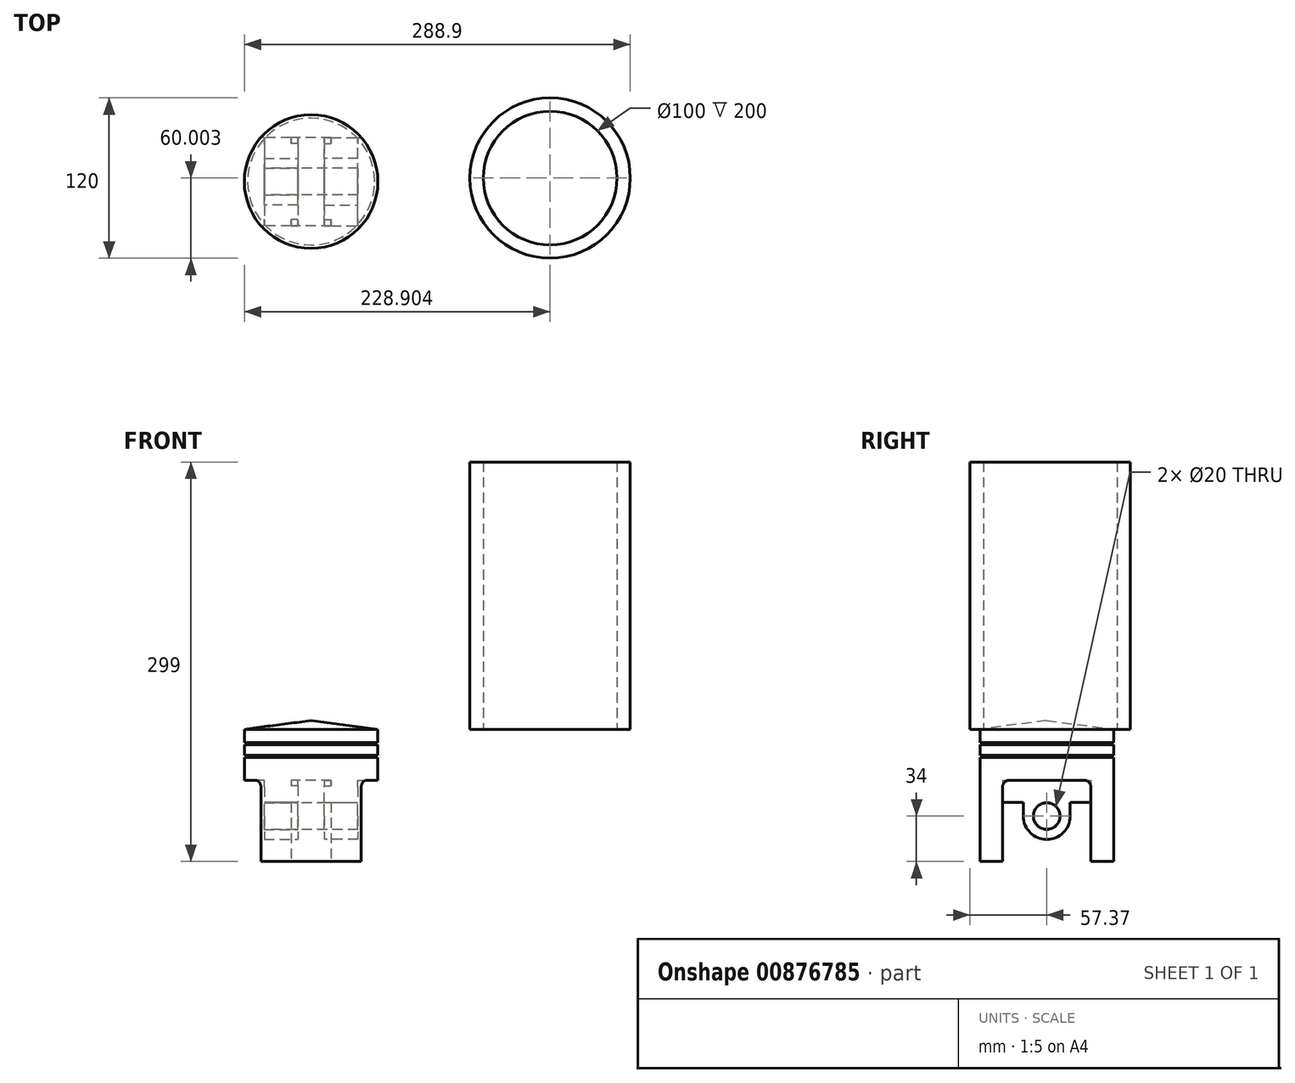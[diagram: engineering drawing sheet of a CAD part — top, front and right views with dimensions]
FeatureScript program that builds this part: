
annotation { "Feature Type Name" : "Feature", "Feature Type Description" : "" }
export const myFeature = defineFeature(function(context is Context, id is Id, definition is map)
    precondition{}
    {
        {
            var Q0;
            Q0=qCreatedBy(makeId("Top.planeOp"),FACE);
            var sketch = newSketch(context, id + "F0", { "sketchPlane" : qUnion([Q0])});
            skCircle(sketch, "E0", {"center": v(0, 0) * mm, "radius": 50 * mm});
            skSolve(sketch);
        }
        {
            var Q0;
            Q0=qCreatedBy(makeId("Right.planeOp"),FACE);
            var sketch = newSketch(context, id + "F1", { "sketchPlane" : qUnion([Q0])});
            skLineSegment(sketch, "E1", {"start": v(0, 0) * mm, "end": v(0, 6.5) * mm});
            skLineSegment(sketch, "E2", {"start": v(0, 6.5) * mm, "end": v(-50, 0) * mm});
            skLineSegment(sketch, "E3", {"start": v(-50, 0) * mm, "end": v(0, 0) * mm});
            skSolve(sketch);
        }
        {
            var Q0;
            Q0=makeQuery(id+"F1.imprint","IMPRINT",FACE,{"disambiguationData":[TD([[makeQuery(id+"F1.imprint","IMPRINT",EDGE,{"derivedFrom":sQuery(id+"F1.wireOp",EDGE,"E1")}),1.0]])]});
            var Q1;
            Q1=sQuery(id+"F1.wireOp",EDGE,"E1");
            revolve(context, id + "F2", {"surfaceOperationType" : NewSurfaceOperationType.NEW, "entities" : qUnion([Q0]), "axis" : qUnion([Q1]), "revolveType" : RevolveType.FULL});
        }
        {
            var Q0;
            Q0 = qSketchRegion(id + "F0", true);
            var Q1;
            Q1=sQuery(id+"F0.wireOp",EDGE,"E0");
            extrude(context, id + "F3", {"entities" : qUnion([Q0]), "surfaceEntities" : qUnion([Q1]), "oppositeDirection" : true, "depth" : 99 * mm, "offsetDistance" : 25 * mm});
        }
        {
            var Q0;
            Q0=qCreatedBy(makeId("Right.planeOp"),FACE);
            var sketch = newSketch(context, id + "F4", { "sketchPlane" : qUnion([Q0])});
            skLineSegment(sketch, "E4.bottom", {"start": v(-50, -10) * mm, "end": v(-47.5, -10) * mm});
            skLineSegment(sketch, "E4.top", {"start": v(-50, -11.5) * mm, "end": v(-47.5, -11.5) * mm});
            skLineSegment(sketch, "E4.left", {"start": v(-50, -10) * mm, "end": v(-50, -11.5) * mm});
            skLineSegment(sketch, "E4.right", {"start": v(-47.5, -10) * mm, "end": v(-47.5, -11.5) * mm});
            skLineSegment(sketch, "E5.bottom", {"start": v(-50, -19.5) * mm, "end": v(-47.5, -19.5) * mm});
            skLineSegment(sketch, "E5.top", {"start": v(-50, -21) * mm, "end": v(-47.5, -21) * mm});
            skLineSegment(sketch, "E5.left", {"start": v(-50, -19.5) * mm, "end": v(-50, -21) * mm});
            skLineSegment(sketch, "E5.right", {"start": v(-47.5, -19.5) * mm, "end": v(-47.5, -21) * mm});
            skSolve(sketch);
        }
        {
            var Q0;
            Q0=qCreatedBy(makeId("Right.planeOp"),FACE);
            var sketch = newSketch(context, id + "F5", { "sketchPlane" : qUnion([Q0])});
            skCircle(sketch, "E6", {"center": v(0, -57.38) * mm, "radius": 10 * mm});
            skSolve(sketch);
        }
        {
            var Q0;
            Q0 = qSketchRegion(id + "F4", true);
            var Q1;
            Q1=makeQuery(id+"F3.opExtrude","SWEPT_FACE",FACE,{"disambiguationData":[OSD([sQuery(id+"F0.wireOp",EDGE,"E0")])]});
            revolve(context, id + "F6", {"operationType" : NewBodyOperationType.REMOVE, "surfaceOperationType" : NewSurfaceOperationType.NEW, "entities" : qUnion([Q0]), "axis" : qUnion([Q1]), "revolveType" : RevolveType.FULL, "oppositeDirection" : true});
        }
        {
            var Q0;
            Q0=qCreatedBy(makeId("Right.planeOp"),FACE);
            cPlane(context, id + "F7", {"entities" : qUnion([Q0]), "cplaneType" : CPlaneType.OFFSET, "offset" : 50 * mm, "width" : 150 * mm, "height" : 150 * mm});
        }
        {
            var Q0;
            Q0=qCreatedBy(makeId("Right.planeOp"),FACE);
            cPlane(context, id + "F8", {"entities" : qUnion([Q0]), "cplaneType" : CPlaneType.OFFSET, "offset" : 50 * mm, "oppositeDirection" : true, "width" : 150 * mm, "height" : 150 * mm});
        }
        {
            var Q0;
            Q0=qCreatedBy(id+"F7.planeOp",FACE);
            var sketch = newSketch(context, id + "F9", { "sketchPlane" : qUnion([Q0])});
            skLineSegment(sketch, "E7.bottom", {"start": v(-33.06, -99) * mm, "end": v(33.06, -99) * mm});
            skLineSegment(sketch, "E7.top", {"start": v(-28.06, -38.19) * mm, "end": v(28.06, -38.19) * mm});
            skLineSegment(sketch, "E7.left", {"start": v(-33.06, -99) * mm, "end": v(-33.06, -43.19) * mm});
            skLineSegment(sketch, "E7.right", {"start": v(33.06, -99) * mm, "end": v(33.06, -43.19) * mm});
            skPoint(sketch, "E8.visualSharp", {"position": v(-33.06, -38.19) * mm});
            skArc(sketch, "E8.filletArc", {"start": v(-28.06, -38.19) * mm, "mid": v(-31.6, -39.65) * mm, "end": v(-33.06, -43.19) * mm});
            skPoint(sketch, "E9.visualSharp", {"position": v(33.06, -38.19) * mm});
            skArc(sketch, "E9.filletArc", {"start": v(33.06, -43.19) * mm, "mid": v(31.6, -39.65) * mm, "end": v(28.06, -38.19) * mm});
            skSolve(sketch);
        }
        {
            var Q0;
            Q0=makeQuery(id+"F9.imprint","IMPRINT",FACE,{"disambiguationData":[TD([[makeQuery(id+"F9.imprint","IMPRINT",EDGE,{"derivedFrom":sQuery(id+"F9.wireOp",EDGE,"E7.bottom")}),1.0]])]});
            extrude(context, id + "F10", {"entities" : qUnion([Q0]), "operationType" : NewBodyOperationType.REMOVE, "oppositeDirection" : true, "depth" : 35 * mm, "offsetDistance" : 25 * mm});
        }
        {
            var Q0;
            Q0=qCreatedBy(id+"F8.planeOp",FACE);
            var sketch = newSketch(context, id + "F11", { "sketchPlane" : qUnion([Q0])});
            skLineSegment(sketch, "E10.bottom", {"start": v(-28.06, -38.19) * mm, "end": v(28.06, -38.19) * mm});
            skLineSegment(sketch, "E10.top", {"start": v(-33.06, -99) * mm, "end": v(33.06, -99) * mm});
            skLineSegment(sketch, "E10.left", {"start": v(-33.06, -43.19) * mm, "end": v(-33.06, -99) * mm});
            skLineSegment(sketch, "E10.right", {"start": v(33.06, -43.19) * mm, "end": v(33.06, -99) * mm});
            skPoint(sketch, "E11.visualSharp", {"position": v(-33.06, -38.19) * mm});
            skArc(sketch, "E11.filletArc", {"start": v(-28.06, -38.19) * mm, "mid": v(-31.6, -39.65) * mm, "end": v(-33.06, -43.19) * mm});
            skPoint(sketch, "E12.visualSharp", {"position": v(33.06, -38.19) * mm});
            skArc(sketch, "E12.filletArc", {"start": v(33.06, -43.19) * mm, "mid": v(31.6, -39.65) * mm, "end": v(28.06, -38.19) * mm});
            skSolve(sketch);
        }
        {
            var Q0;
            Q0=makeQuery(id+"F11.imprint","IMPRINT",FACE,{"disambiguationData":[TD([[makeQuery(id+"F11.imprint","IMPRINT",EDGE,{"derivedFrom":sQuery(id+"F11.wireOp",EDGE,"E10.bottom")}),-1.0]])]});
            extrude(context, id + "F12", {"entities" : qUnion([Q0]), "operationType" : NewBodyOperationType.REMOVE, "depth" : 35 * mm, "offsetDistance" : 25 * mm});
        }
        {
            var Q0;
            Q0=makeQuery(id+"F5.imprint","IMPRINT",FACE,{"disambiguationData":[TD([[makeQuery(id+"F5.imprint","IMPRINT",EDGE,{"derivedFrom":sQuery(id+"F5.wireOp",EDGE,"E6")}),1.0]])]});
            var Q1;
            Q1=sQuery(id+"F5.wireOp",EDGE,"E6");
            extrude(context, id + "F13", {"entities" : qUnion([Q0]), "surfaceEntities" : qUnion([Q1]), "endBound" : BoundingType.SYMMETRIC, "depth" : 39.6 * mm, "offsetDistance" : 25 * mm});
        }
        {
            var Q0;
            Q0=makeQuery(id+"F13.opExtrude","SWEPT_BODY",BODY,{"disambiguationData":[OSD([sQuery(id+"F5.wireOp",EDGE,"E6")])]});
            var Q1;
            Q1=makeQuery(id+"F3.opExtrude","SWEPT_BODY",BODY,{"disambiguationData":[OSD([sQuery(id+"F0.wireOp",EDGE,"E0")])]});
            booleanBodies(context, id + "F14", {"operationType" : BooleanOperationType.SUBTRACTION, "tools" : qUnion([Q0]), "targets" : qUnion([Q1])});
        }
        {
            var Q0;
            Q0=makeQuery(id+"F3.opExtrude","CAP_FACE",FACE,{"disambiguationData":[OSD([sQuery(id+"F0.wireOp",EDGE,"E0")])],"isStart":false});
            var sketch = newSketch(context, id + "F15", { "sketchPlane" : qUnion([Q0])});
            skLineSegment(sketch, "E13.bottom", {"start": v(15, -33) * mm, "end": v(-15, -33) * mm});
            skLineSegment(sketch, "E13.top", {"start": v(15, 33) * mm, "end": v(-15, 33) * mm});
            skLineSegment(sketch, "E13.left", {"start": v(15, -33) * mm, "end": v(15, 33) * mm});
            skLineSegment(sketch, "E13.right", {"start": v(-15, -33) * mm, "end": v(-15, 33) * mm});
            skSolve(sketch);
        }
        {
            var Q0;
            Q0 = qSketchRegion(id + "F15", true);
            extrude(context, id + "F16", {"entities" : qUnion([Q0]), "operationType" : NewBodyOperationType.REMOVE, "oppositeDirection" : true, "depth" : 60.8 * mm, "offsetDistance" : 25 * mm});
        }
        {
            var Q0;
            Q0 = qSketchRegion(id + "F15", true);
            extrude(context, id + "F17", {"entities" : qUnion([Q0]), "operationType" : NewBodyOperationType.REMOVE, "oppositeDirection" : true, "depth" : 60 * mm, "offsetDistance" : 25 * mm});
        }
        {
            var Q0;
            Q0=qCreatedBy(makeId("Right.planeOp"),FACE);
            cPlane(context, id + "F18", {"entities" : qUnion([Q0]), "cplaneType" : CPlaneType.OFFSET, "offset" : 10 * mm, "width" : 150 * mm, "height" : 150 * mm});
        }
        {
            var Q0;
            Q0=qCreatedBy(makeId("Right.planeOp"),FACE);
            cPlane(context, id + "F19", {"entities" : qUnion([Q0]), "cplaneType" : CPlaneType.OFFSET, "offset" : 10 * mm, "oppositeDirection" : true, "width" : 150 * mm, "height" : 150 * mm});
        }
        {
            var Q0;
            Q0=qCreatedBy(id+"F18.planeOp",FACE);
            var sketch = newSketch(context, id + "F20", { "sketchPlane" : qUnion([Q0])});
            skCircle(sketch, "E14", {"center": v(0, -65) * mm, "radius": 10 * mm});
            skArc(sketch, "E15", {"start": v(-17.5, -65) * mm, "mid": v(0, -82.5) * mm, "end": v(17.5, -65) * mm});
            skLineSegment(sketch, "E16", {"start": v(-17.5, -65) * mm, "end": v(-17.5, -38.2) * mm});
            skLineSegment(sketch, "E17", {"start": v(17.5, -65) * mm, "end": v(17.5, -38.2) * mm});
            skLineSegment(sketch, "E18", {"start": v(17.5, -38.2) * mm, "end": v(-17.5, -38.2) * mm});
            skSolve(sketch);
        }
        {
            var Q0;
            Q0=qCreatedBy(id+"F19.planeOp",FACE);
            var sketch = newSketch(context, id + "F21", { "sketchPlane" : qUnion([Q0])});
            skCircle(sketch, "E19", {"center": v(0, -65) * mm, "radius": 10 * mm});
            skArc(sketch, "E20", {"start": v(-17.5, -65) * mm, "mid": v(0, -82.5) * mm, "end": v(17.5, -65) * mm});
            skLineSegment(sketch, "E21", {"start": v(-17.5, -65) * mm, "end": v(-17.5, -38.2) * mm});
            skLineSegment(sketch, "E22", {"start": v(17.5, -65) * mm, "end": v(17.5, -38.2) * mm});
            skLineSegment(sketch, "E23", {"start": v(17.5, -38.2) * mm, "end": v(-17.5, -38.2) * mm});
            skSolve(sketch);
        }
        {
            var Q0;
            Q0 = qSketchRegion(id + "F20", true);
            extrude(context, id + "F22", {"entities" : qUnion([Q0]), "operationType" : NewBodyOperationType.ADD, "depth" : 25 * mm, "offsetDistance" : 25 * mm});
        }
        {
            var Q0;
            Q0 = qSketchRegion(id + "F21", true);
            extrude(context, id + "F23", {"entities" : qUnion([Q0]), "operationType" : NewBodyOperationType.ADD, "oppositeDirection" : true, "depth" : 25 * mm, "offsetDistance" : 25 * mm});
        }
        {
            var Q0;
            Q0=makeQuery(id+"F23.opExtrude","CAP_FACE",FACE,{"disambiguationData":[OSD([sQuery(id+"F21.wireOp",EDGE,"E19"),sQuery(id+"F21.wireOp",EDGE,"E20"),sQuery(id+"F21.wireOp",EDGE,"E21"),sQuery(id+"F21.wireOp",EDGE,"E22"),sQuery(id+"F21.wireOp",EDGE,"E23")])],"isStart":false});
            var sketch = newSketch(context, id + "F24", { "sketchPlane" : qUnion([Q0])});
            skLineSegment(sketch, "E24.bottom", {"start": v(-28.06, -38.19) * mm, "end": v(28.06, -38.19) * mm});
            skLineSegment(sketch, "E24.top", {"start": v(-33.06, -54.79) * mm, "end": v(33.06, -54.79) * mm});
            skLineSegment(sketch, "E24.left", {"start": v(-33.06, -43.19) * mm, "end": v(-33.06, -54.79) * mm});
            skLineSegment(sketch, "E24.right", {"start": v(33.06, -43.19) * mm, "end": v(33.06, -54.79) * mm});
            skPoint(sketch, "E25.visualSharp", {"position": v(-33.06, -38.19) * mm});
            skArc(sketch, "E25.filletArc", {"start": v(-28.06, -38.19) * mm, "mid": v(-31.6, -39.65) * mm, "end": v(-33.06, -43.19) * mm});
            skPoint(sketch, "E26.visualSharp", {"position": v(33.06, -38.19) * mm});
            skArc(sketch, "E26.filletArc", {"start": v(33.06, -43.19) * mm, "mid": v(31.6, -39.65) * mm, "end": v(28.06, -38.19) * mm});
            skSolve(sketch);
        }
        {
            var Q0;
            Q0=qCreatedBy(makeId("Right.planeOp"),FACE);
            cPlane(context, id + "F25", {"entities" : qUnion([Q0]), "cplaneType" : CPlaneType.OFFSET, "offset" : 35 * mm, "width" : 150 * mm, "height" : 150 * mm});
        }
        {
            var Q0;
            Q0=qCreatedBy(id+"F25.planeOp",FACE);
            var sketch = newSketch(context, id + "F26", { "sketchPlane" : qUnion([Q0])});
            skLineSegment(sketch, "E27.bottom", {"start": v(-28.06, -38.19) * mm, "end": v(28.06, -38.19) * mm});
            skLineSegment(sketch, "E27.top", {"start": v(-33.06, -54.79) * mm, "end": v(33.06, -54.79) * mm});
            skLineSegment(sketch, "E27.left", {"start": v(-33.06, -43.19) * mm, "end": v(-33.06, -54.79) * mm});
            skLineSegment(sketch, "E27.right", {"start": v(33.06, -43.19) * mm, "end": v(33.06, -54.79) * mm});
            skPoint(sketch, "E28.visualSharp", {"position": v(-33.06, -38.19) * mm});
            skArc(sketch, "E28.filletArc", {"start": v(-28.06, -38.19) * mm, "mid": v(-31.6, -39.65) * mm, "end": v(-33.06, -43.19) * mm});
            skPoint(sketch, "E29.visualSharp", {"position": v(33.06, -38.19) * mm});
            skArc(sketch, "E29.filletArc", {"start": v(33.06, -43.19) * mm, "mid": v(31.6, -39.65) * mm, "end": v(28.06, -38.19) * mm});
            skSolve(sketch);
        }
        {
            var Q0;
            Q0 = qSketchRegion(id + "F24", true);
            extrude(context, id + "F27", {"entities" : qUnion([Q0]), "operationType" : NewBodyOperationType.ADD, "oppositeDirection" : true, "depth" : 25 * mm, "offsetDistance" : 25 * mm});
        }
        {
            var Q0;
            Q0 = qSketchRegion(id + "F26", true);
            extrude(context, id + "F28", {"entities" : qUnion([Q0]), "operationType" : NewBodyOperationType.ADD, "oppositeDirection" : true, "depth" : 25 * mm, "offsetDistance" : 25 * mm});
        }
        {
            var Q0;
            Q0=qCreatedBy(makeId("Right.planeOp"),FACE);
            var sketch = newSketch(context, id + "F29", { "sketchPlane" : qUnion([Q0])});
            skCircle(sketch, "E30", {"center": v(0, -65) * mm, "radius": 9.95 * mm});
            skSolve(sketch);
        }
        {
            var Q0;
            Q0 = qSketchRegion(id + "F29", true);
            extrude(context, id + "F30", {"entities" : qUnion([Q0]), "endBound" : BoundingType.SYMMETRIC, "depth" : 70 * mm, "offsetDistance" : 25 * mm});
        }
        {
            var Q0;
            Q0=qCreatedBy(makeId("Top.planeOp"),FACE);
            var sketch = newSketch(context, id + "F31", { "sketchPlane" : qUnion([Q0])});
            skCircle(sketch, "E31", {"center": v(170.9, -5.84) * mm, "radius": 60 * mm});
            skSolve(sketch);
        }
        {
            var Q0;
            Q0=makeQuery(id+"F31.imprint","IMPRINT",FACE,{"disambiguationData":[TD([[makeQuery(id+"F31.imprint","IMPRINT",EDGE,{"derivedFrom":sQuery(id+"F31.wireOp",EDGE,"E31")}),1.0]])]});
            extrude(context, id + "F32", {"entities" : qUnion([Q0]), "depth" : 250 * mm, "offsetDistance" : 25 * mm});
        }
        {
            var Q0;
            Q0=makeQuery(id+"F32.opExtrude","CAP_FACE",FACE,{"disambiguationData":[OSD([sQuery(id+"F31.wireOp",EDGE,"E31")])],"isStart":false});
            var sketch = newSketch(context, id + "F33", { "sketchPlane" : qUnion([Q0])});
            skCircle(sketch, "E32", {"center": v(170.9, -5.84) * mm, "radius": 50 * mm});
            skSolve(sketch);
        }
        {
            var Q0;
            Q0=makeQuery(id+"F33.imprint","IMPRINT",FACE,{"disambiguationData":[TD([[makeQuery(id+"F33.imprint","IMPRINT",EDGE,{"derivedFrom":sQuery(id+"F33.wireOp",EDGE,"E32")}),1.0]])]});
            extrude(context, id + "F34", {"entities" : qUnion([Q0]), "operationType" : NewBodyOperationType.REMOVE, "oppositeDirection" : true, "depth" : 250 * mm, "offsetDistance" : 25 * mm});
        }
        {
            var Q0;
            Q0=makeQuery(id+"F32.opExtrude","SWEPT_BODY",BODY,{"disambiguationData":[OSD([sQuery(id+"F31.wireOp",EDGE,"E31")])]});
            deleteBodies(context, id + "F35", {"entities" : qUnion([Q0])});
        }
        {
            var Q0;
            Q0=qCreatedBy(makeId("Top.planeOp"),FACE);
            var sketch = newSketch(context, id + "F36", { "sketchPlane" : qUnion([Q0])});
            skCircle(sketch, "E33", {"center": v(178.9, 2.63) * mm, "radius": 60 * mm});
            skCircle(sketch, "E34", {"center": v(178.9, 2.63) * mm, "radius": 50 * mm});
            skSolve(sketch);
        }
        {
            var Q0;
            Q0=makeQuery(id+"F36.imprint","IMPRINT",FACE,{"disambiguationData":[TD([[makeQuery(id+"F36.imprint","IMPRINT",EDGE,{"derivedFrom":sQuery(id+"F36.wireOp",EDGE,"E33")}),1.0]])]});
            extrude(context, id + "F37", {"entities" : qUnion([Q0]), "depth" : 200 * mm, "offsetDistance" : 25 * mm});
        }
    });
